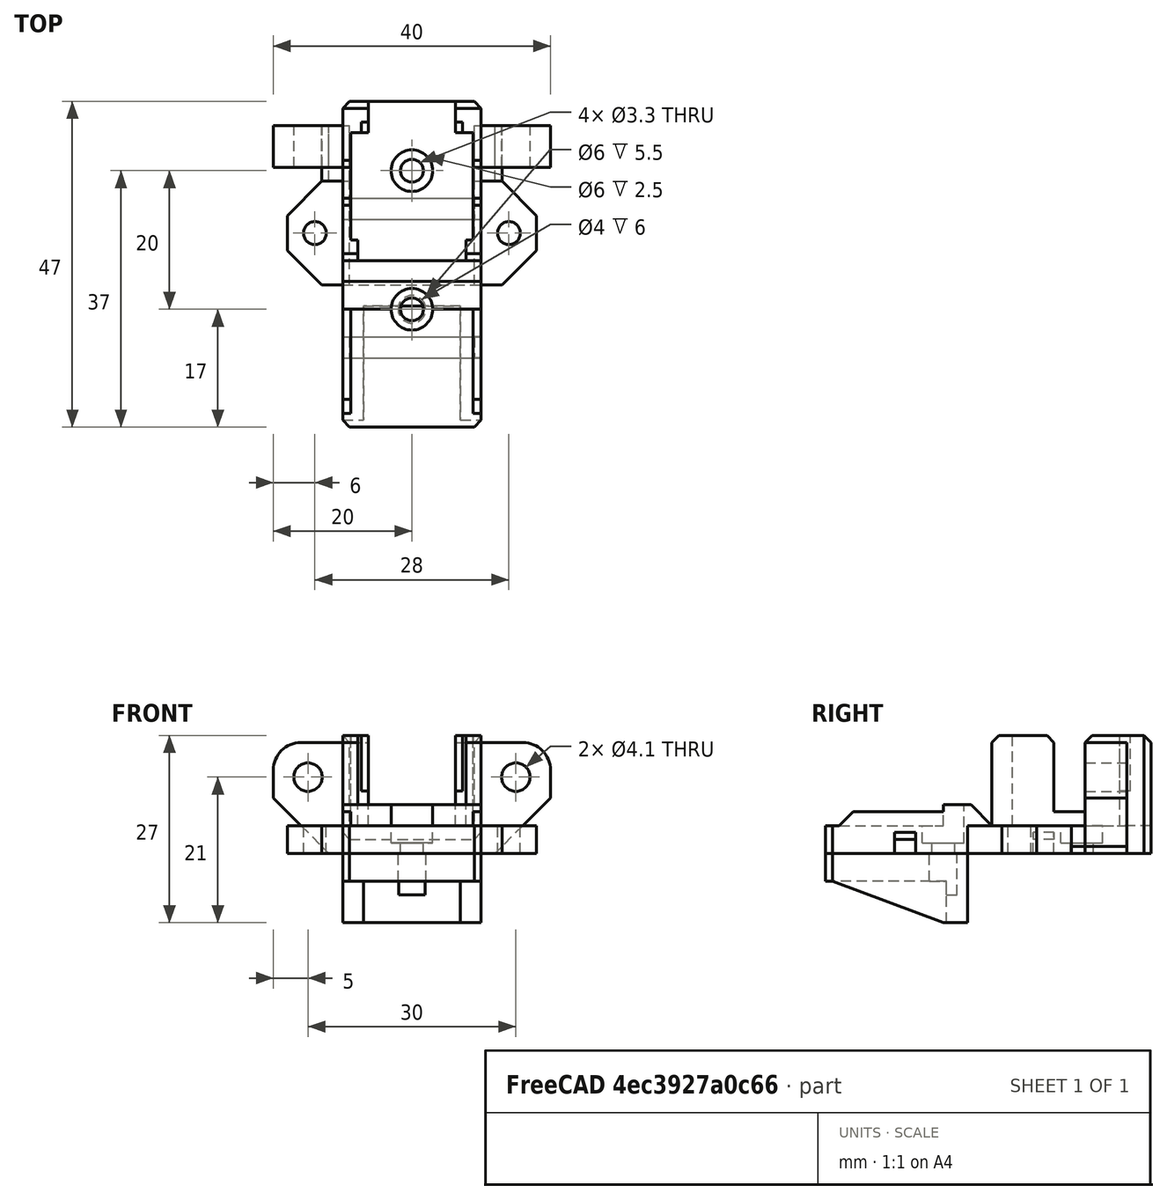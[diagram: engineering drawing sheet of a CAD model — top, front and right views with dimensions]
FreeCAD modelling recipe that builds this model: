
FCSTD DOCUMENT  (FreeCAD 0.18R16146 (Git))
Label: power-plug
License: All rights reserved
LicenseURL: http://en.wikipedia.org/wiki/All_rights_reserved
objects: Part::Box×12, Part::MultiFuse×7, Part::Chamfer×7, Part::Cylinder×5, Part::Cut×5, Part::Feature×2, App::DocumentObjectGroup×2, Part::Fillet×1
note: 39 computed .brp shape members not serialized (recipe doc carries the construction recipe); baked Part::Feature solids carry a one-line shape summary decoded from their .brp

FEATURE [Part::Feature] Chamfer003001001  label="plug-holder-2-pin"
  Placement = pos=(-10,21.5,1.2e-14) rot=(0,0,-1;1.5708rad)
  shape: bbox 20 x 47 x 17 mm, 63 faces (baked)
FEATURE [Part::Box] Box  label="Cube"
  AttacherType = Attacher::AttachEngine3D
  Height = 4
  Length = 9
  Placement = pos=(9,-5,0) rot=(0,0,1;0rad)
  Width = 15
FEATURE [Part::Box] Box001  label="Cube001"
  AttacherType = Attacher::AttachEngine3D
  Height = 4
  Length = 9
  Placement = pos=(-18,-5,0) rot=(0,0,1;0rad)
  Width = 15
FEATURE [Part::Cylinder] Cylinder
  Angle = 360
  AttacherType = Attacher::AttachEngine3D
  Height = 10
  Placement = pos=(-14,2.5,0) rot=(0,0,1;0rad)
  Radius = 1.65
FEATURE [Part::Cylinder] Cylinder001
  Angle = 360
  AttacherType = Attacher::AttachEngine3D
  Height = 10
  Placement = pos=(14,2.5,0) rot=(0,0,1;0rad)
  Radius = 1.65
FEATURE [Part::MultiFuse] Fusion
  Shapes = -> [Cylinder001,Cylinder]
FEATURE [Part::MultiFuse] Fusion001
  Shapes = -> [Box001,Box]
FEATURE [Part::Chamfer] Chamfer
  Base = -> Fusion001
  Edges = 4 edges r=5: [Edge1,Edge3,Edge17,Edge19]
FEATURE [Part::Cut] Cut
  Base = -> Chamfer
  Tool = -> Fusion
FEATURE [Part::Box] Box003  label="Cube003"
  AttacherType = Attacher::AttachEngine3D
  Height = 12
  Length = 22
  Placement = pos=(-11,7.5,6) rot=(0,0,1;0rad)
  Width = 4.5
FEATURE [Part::Cut] Cut001
  Base = -> Chamfer003001001
  Tool = -> Box003
FEATURE [Part::Chamfer] Chamfer003001002
  Base = -> Cut001
  Edges = 4 edges r=1: [Edge70,Edge77,Edge140,Edge145]
FEATURE [Part::Box] Box004  label="Cube004"
  AttacherType = Attacher::AttachEngine3D
  Height = 16
  Length = 11
  Placement = pos=(9,12,0) rot=(0,0,1;0rad)
  Width = 5
FEATURE [Part::Box] Box005  label="Cube005"
  AttacherType = Attacher::AttachEngine3D
  Height = 16
  Length = 11
  Placement = pos=(-20,12,0) rot=(0,0,1;0rad)
  Width = 5
FEATURE [Part::MultiFuse] Fusion002
  Shapes = -> [Box004,Box005]
FEATURE [Part::Chamfer] Chamfer003001003
  Base = -> Fusion002
  Edges = 2 edges r=8: [Edge8,Edge16]
FEATURE [Part::Fillet] Fillet
  Base = -> Chamfer003001003
  Edges = 2 edges r=4: [Edge3,Edge18]
FEATURE [Part::Feature] Fillet001
  Placement = pos=(0,1,0) rot=(0,0,1;0rad)
  shape: bbox 40 x 5 x 16 mm, 16 faces, 2 solids (baked)
FEATURE [Part::MultiFuse] Fusion003
  Shapes = -> [Fillet,Fillet001]
FEATURE [Part::Cylinder] Cylinder003
  Angle = 360
  AttacherType = Attacher::AttachEngine3D
  Height = 9
  Placement = pos=(15,10.5,11) rot=(-1,0,0;1.5708rad)
  Radius = 2.05
FEATURE [Part::Cylinder] Cylinder004
  Angle = 360
  AttacherType = Attacher::AttachEngine3D
  Height = 9
  Placement = pos=(-15,10.5,11) rot=(-1,0,0;1.5708rad)
  Radius = 2.05
FEATURE [Part::Box] Box006  label="Cube006"
  AttacherType = Attacher::AttachEngine3D
  Height = 4
  Length = 4
  Placement = pos=(-13,10,0) rot=(0,0,1;0rad)
  Width = 8
FEATURE [Part::Box] Box007  label="Cube007"
  AttacherType = Attacher::AttachEngine3D
  Height = 4
  Length = 4
  Placement = pos=(9,10,0) rot=(0,0,1;0rad)
  Width = 8
FEATURE [Part::Chamfer] Chamfer003001004
  Base = -> Box007
  Edges = 1 edges r=1: [Edge8]
FEATURE [Part::Chamfer] Chamfer003001005
  Base = -> Box006
  Edges = 1 edges r=1: [Edge4]
FEATURE [Part::Box] Box008  label="Cube008"
  AttacherType = Attacher::AttachEngine3D
  Height = 14
  Length = 17.6
  Placement = pos=(-8.8,7,4) rot=(0,0,1;0rad)
  Width = 10
FEATURE [Part::Cut] Cut003
  Base = -> Chamfer003001002
  Tool = -> Box008
FEATURE [Part::MultiFuse] Fusion004
  Shapes = -> [Cylinder003,Cylinder004]
FEATURE [Part::Cut] Cut004
  Base = -> Fusion003
  Tool = -> Fusion004
FEATURE [App::DocumentObjectGroup] Group  label="main"
  Group = -> [Cut,Chamfer003001004,Chamfer003001005,Cut003,Cut004]
FEATURE [App::DocumentObjectGroup] Group001  label="support"
FEATURE [Part::Box] Box009  label="Cube009"
  AttacherType = Attacher::AttachEngine3D
  Height = 4
  Length = 20
  Placement = pos=(-10,-25.5,-4) rot=(0,0,1;0rad)
  Width = 20.5
FEATURE [Part::Box] Box010  label="Cube010"
  AttacherType = Attacher::AttachEngine3D
  Height = 10
  Length = 20
  Placement = pos=(-10,-8,-10) rot=(0,0,1;0rad)
  Width = 3
FEATURE [Part::Box] Box011  label="Cube011"
  AttacherType = Attacher::AttachEngine3D
  Height = 10
  Length = 3
  Placement = pos=(-10,-24.5,-10) rot=(0,0,1;0rad)
  Width = 17
FEATURE [Part::Box] Box012  label="Cube012"
  AttacherType = Attacher::AttachEngine3D
  Height = 10
  Length = 3
  Placement = pos=(7,-24.5,-10) rot=(0,0,1;0rad)
  Width = 17
FEATURE [Part::Chamfer] Chamfer003001006
  Base = -> Box009
  Edges = 2 edges r=1: [Edge1,Edge5]
FEATURE [Part::MultiFuse] Fusion005
  Shapes = -> [Box011,Box012]
FEATURE [Part::Chamfer] Chamfer003001007
  Base = -> Fusion005
  Edges = 2 edges: [Edge9 r1=6 r2=16,Edge21 r1=6 r2=16]
FEATURE [Part::MultiFuse] Fusion006
  Shapes = -> [Chamfer003001007,Chamfer003001006,Box010]
FEATURE [Part::Cylinder] Cylinder005
  Angle = 360
  AttacherType = Attacher::AttachEngine3D
  Height = 10
  Placement = pos=(0,-8.5,-6) rot=(0,0,1;0rad)
  Radius = 2
FEATURE [Part::Cut] Cut005
  Base = -> Fusion006
  Tool = -> Cylinder005
